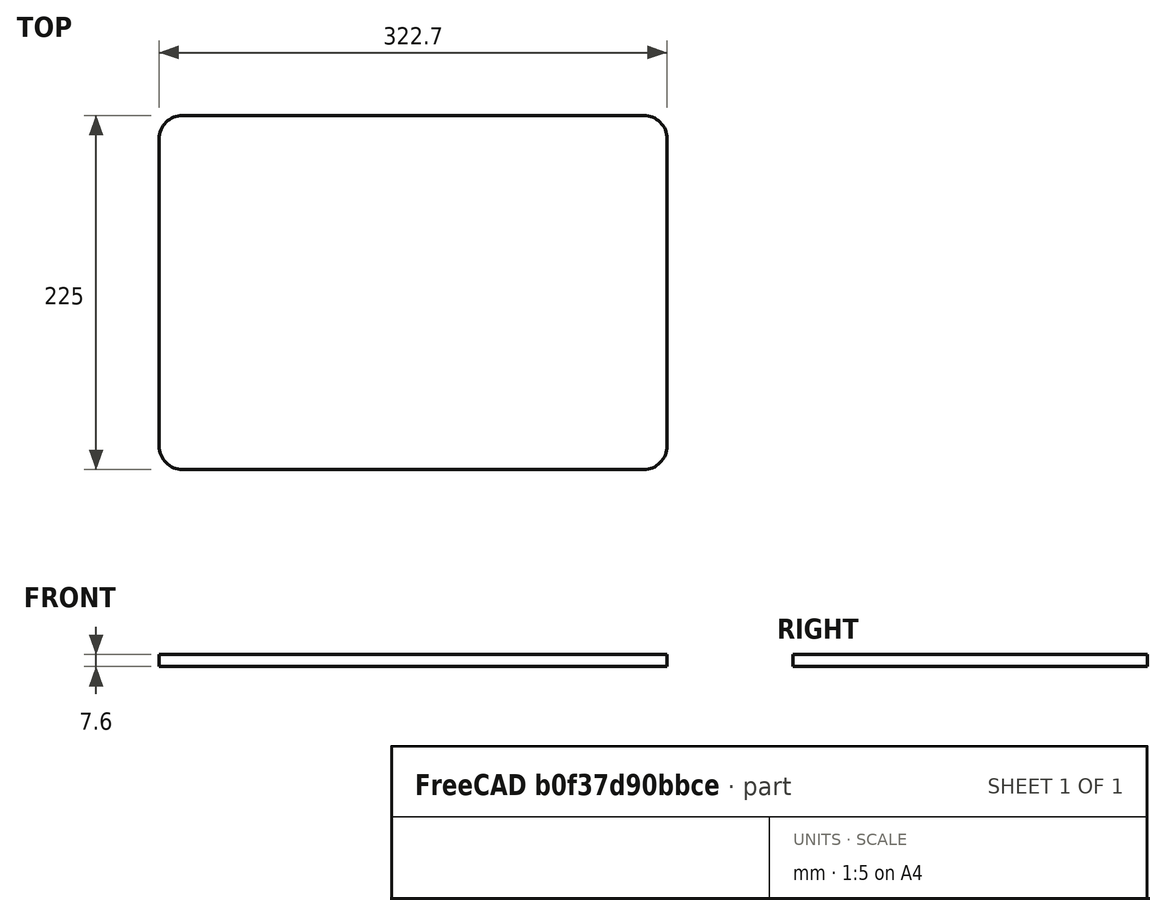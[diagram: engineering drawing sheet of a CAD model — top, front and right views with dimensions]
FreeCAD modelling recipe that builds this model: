
FCSTD DOCUMENT  (FreeCAD 0.16RUnknown)
Label: laptop_stand
License: All rights reserved
LicenseURL: http://en.wikipedia.org/wiki/All_rights_reserved
objects: PartDesign::Fillet×4, Part::Part2DObjectPython×1, Part::Extrusion×1
note: 6 computed .brp shape members not serialized (recipe doc carries the construction recipe); baked Part::Feature solids carry a one-line shape summary decoded from their .brp

FEATURE [Part::Part2DObjectPython] Rectangle  # Draft 2D object (typed FeaturePython)
  ChamferSize = 0
  Columns = 1
  FilletRadius = 0
  Height = 225
  Length = 322.7
  MakeFace = true
  Rows = 1
FEATURE [Part::Extrusion] Extrude
  Base = -> Rectangle
  Dir = (0,0,7.6)
  Solid = true
FEATURE [PartDesign::Fillet] Fillet
  Base = -> Extrude [Edge2]
  Radius = 15
FEATURE [PartDesign::Fillet] Fillet001
  Base = -> Fillet [Edge3]
  Radius = 15
FEATURE [PartDesign::Fillet] Fillet002
  Base = -> Fillet001 [Edge18]
  Radius = 15
FEATURE [PartDesign::Fillet] Fillet003
  Base = -> Fillet002 [Edge15]
  Radius = 15
